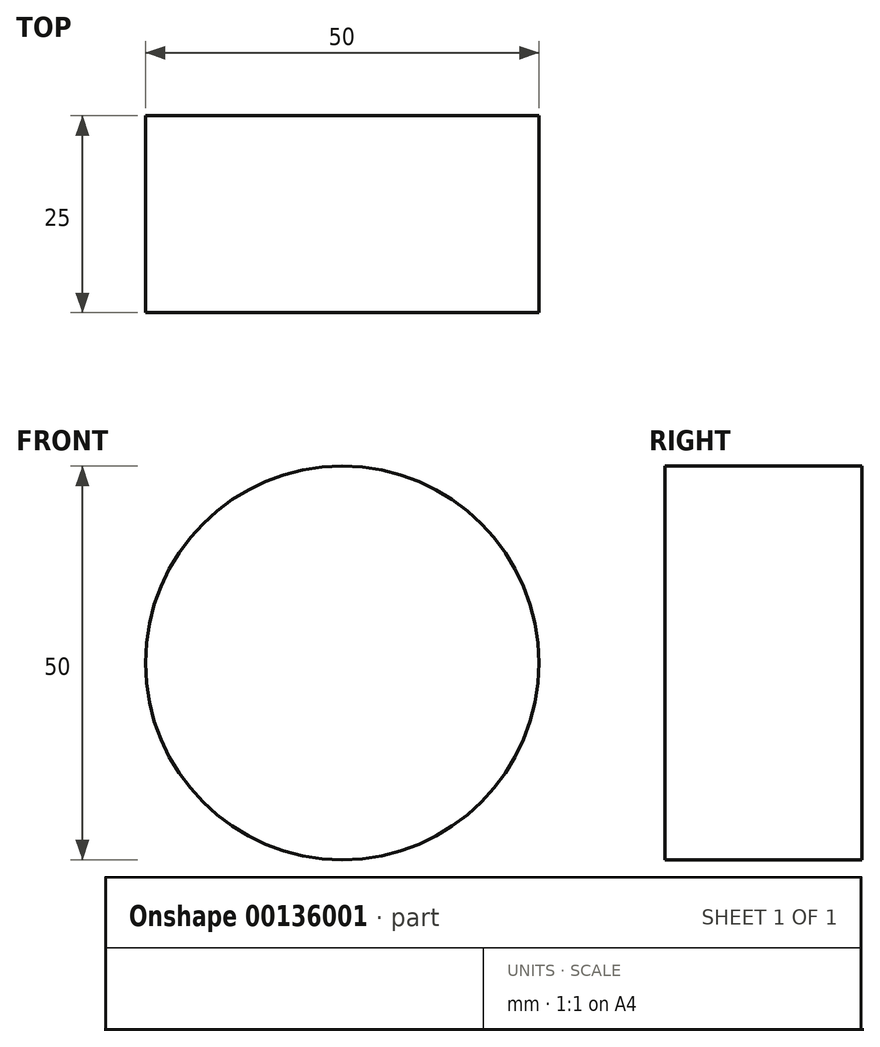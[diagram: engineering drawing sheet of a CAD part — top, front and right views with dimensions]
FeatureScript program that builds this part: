
annotation { "Feature Type Name" : "Feature", "Feature Type Description" : "" }
export const myFeature = defineFeature(function(context is Context, id is Id, definition is map)
    precondition{}
    {
        {
            var Q0;
            Q0=qCreatedBy(makeId("Front.planeOp"),FACE);
            var sketch = newSketch(context, id + "F0", { "sketchPlane" : qUnion([Q0])});
            skCircle(sketch, "E0", {"center": v(0, 0) * mm, "radius": 25 * mm});
            skSolve(sketch);
        }
        {
            var Q0;
            Q0 = qSketchRegion(id + "F0", true);
            extrude(context, id + "F1", {"entities" : qUnion([Q0]), "depth" : 25 * mm});
        }
    });
